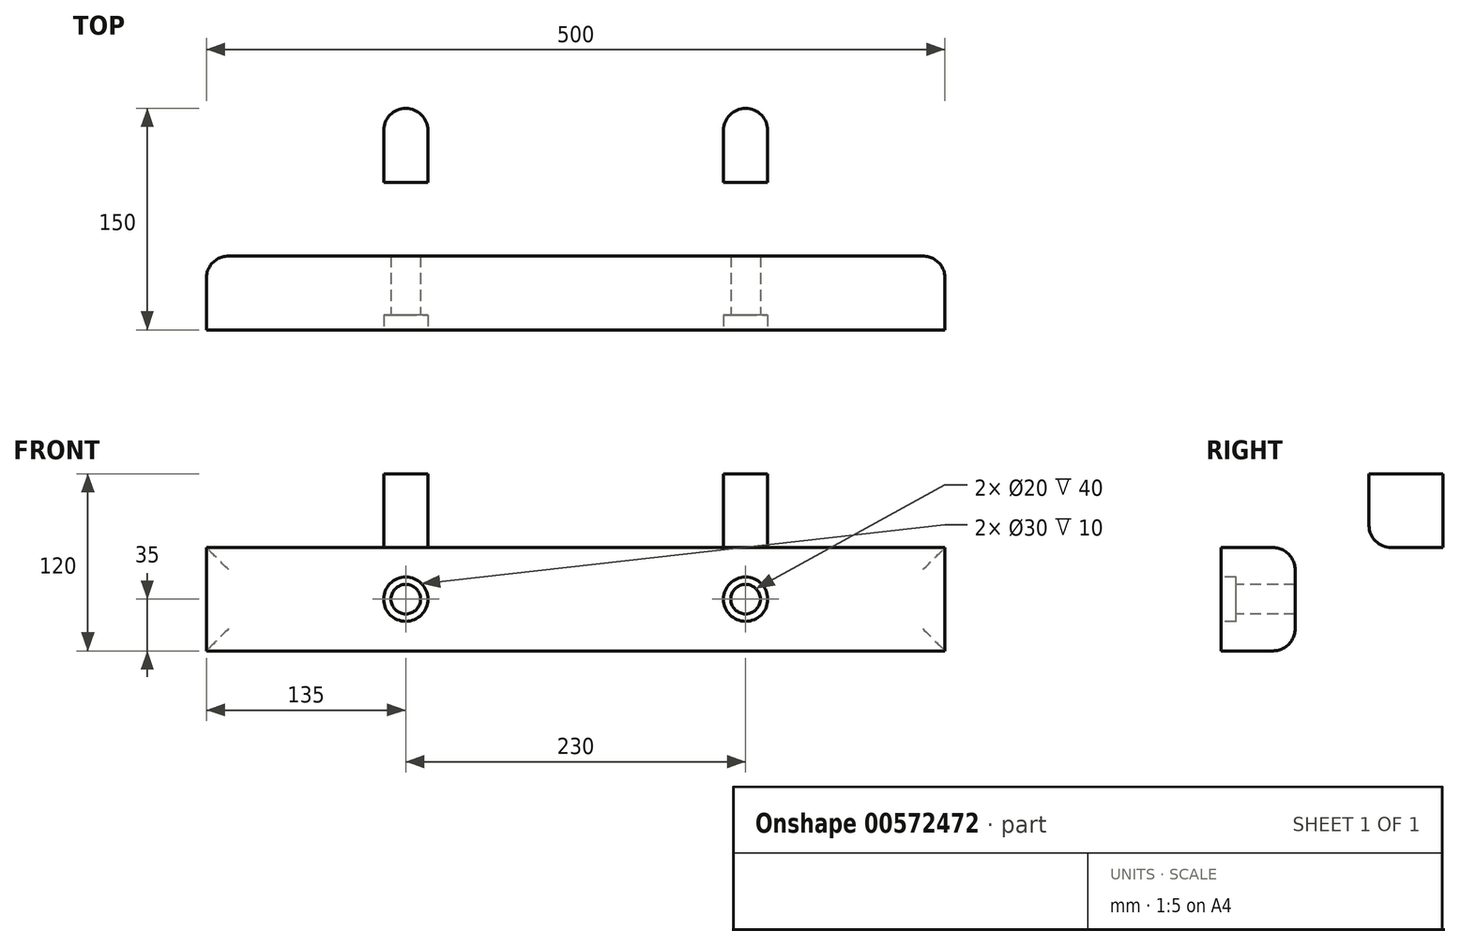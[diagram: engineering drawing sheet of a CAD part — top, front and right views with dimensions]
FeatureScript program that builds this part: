
annotation { "Feature Type Name" : "Feature", "Feature Type Description" : "" }
export const myFeature = defineFeature(function(context is Context, id is Id, definition is map)
    precondition{}
    {
        {
            var Q0;
            Q0=qCreatedBy(makeId("Top.planeOp"),FACE);
            var sketch = newSketch(context, id + "F0", { "sketchPlane" : qUnion([Q0])});
            skLineSegment(sketch, "E0.bottom", {"start": v(-250, 0) * mm, "end": v(250, 0) * mm});
            skLineSegment(sketch, "E0.top", {"start": v(-250, -50) * mm, "end": v(250, -50) * mm});
            skLineSegment(sketch, "E0.left", {"start": v(-250, 0) * mm, "end": v(-250, -50) * mm});
            skLineSegment(sketch, "E0.right", {"start": v(250, 0) * mm, "end": v(250, -50) * mm});
            skLineSegment(sketch, "E1.bottom", {"start": v(-130, 0) * mm, "end": v(-100, 0) * mm});
            skLineSegment(sketch, "E1.top", {"start": v(-130, 100) * mm, "end": v(-100, 100) * mm});
            skLineSegment(sketch, "E1.left", {"start": v(-130, 0) * mm, "end": v(-130, 100) * mm});
            skLineSegment(sketch, "E1.right", {"start": v(-100, 0) * mm, "end": v(-100, 100) * mm});
            skLineSegment(sketch, "E2.bottom", {"start": v(100, 0) * mm, "end": v(130, 0) * mm});
            skLineSegment(sketch, "E2.top", {"start": v(100, 100) * mm, "end": v(130, 100) * mm});
            skLineSegment(sketch, "E2.left", {"start": v(100, 0) * mm, "end": v(100, 100) * mm});
            skLineSegment(sketch, "E2.right", {"start": v(130, 0) * mm, "end": v(130, 100) * mm});
            skSolve(sketch);
        }
        {
            var Q0;
            Q0=makeQuery(id+"F0.imprint","IMPRINT",FACE,{"disambiguationData":[TD([[makeQuery(id+"F0.imprint","IMPRINT",EDGE,{"derivedFrom":sQuery(id+"F0.wireOp",EDGE,"E0.top")}),1.0]])]});
            var Q1;
            Q1=makeQuery(id+"F0.imprint","IMPRINT",FACE,{"disambiguationData":[TD([[makeQuery(id+"F0.imprint","IMPRINT",EDGE,{"derivedFrom":sQuery(id+"F0.wireOp",EDGE,"E1.bottom")}),1.0]])]});
            var Q2;
            Q2=makeQuery(id+"F0.imprint","IMPRINT",FACE,{"disambiguationData":[TD([[makeQuery(id+"F0.imprint","IMPRINT",EDGE,{"derivedFrom":sQuery(id+"F0.wireOp",EDGE,"E2.bottom")}),1.0]])]});
            extrude(context, id + "F1", {"entities" : qUnion([Q0, Q1, Q2]), "depth" : 70 * mm, "offsetDistance" : 25 * mm});
        }
        {
            var Q0;
            Q0=makeQuery(id+"F1.opExtrude","CAP_FACE",FACE,{"disambiguationData":[OSD([sQuery(id+"F0.wireOp",EDGE,"E0.bottom"),sQuery(id+"F0.wireOp",EDGE,"E0.top"),sQuery(id+"F0.wireOp",EDGE,"E0.left"),sQuery(id+"F0.wireOp",EDGE,"E0.right"),sQuery(id+"F0.wireOp",EDGE,"E1.top"),sQuery(id+"F0.wireOp",EDGE,"E1.left"),sQuery(id+"F0.wireOp",EDGE,"E1.right"),sQuery(id+"F0.wireOp",EDGE,"E2.top"),sQuery(id+"F0.wireOp",EDGE,"E2.left"),sQuery(id+"F0.wireOp",EDGE,"E2.right")])],"isStart":false});
            var sketch = newSketch(context, id + "F2", { "sketchPlane" : qUnion([Q0])});
            skLineSegment(sketch, "E3.bottom", {"start": v(-130, 100) * mm, "end": v(-100, 100) * mm});
            skLineSegment(sketch, "E3.top", {"start": v(-130, 50) * mm, "end": v(-100, 50) * mm});
            skLineSegment(sketch, "E3.left", {"start": v(-130, 100) * mm, "end": v(-130, 50) * mm});
            skLineSegment(sketch, "E3.right", {"start": v(-100, 100) * mm, "end": v(-100, 50) * mm});
            skLineSegment(sketch, "E4.bottom", {"start": v(100, 100) * mm, "end": v(130, 100) * mm});
            skLineSegment(sketch, "E4.top", {"start": v(100, 50) * mm, "end": v(130, 50) * mm});
            skLineSegment(sketch, "E4.left", {"start": v(100, 100) * mm, "end": v(100, 50) * mm});
            skLineSegment(sketch, "E4.right", {"start": v(130, 100) * mm, "end": v(130, 50) * mm});
            skSolve(sketch);
        }
        {
            var Q0;
            Q0=makeQuery(id+"F2.imprint","IMPRINT",FACE,{"disambiguationData":[TD([[makeQuery(id+"F2.imprint","IMPRINT",EDGE,{"derivedFrom":sQuery(id+"F2.wireOp",EDGE,"E3.bottom")}),-1.0]])]});
            var Q1;
            Q1=makeQuery(id+"F2.imprint","IMPRINT",FACE,{"disambiguationData":[TD([[makeQuery(id+"F2.imprint","IMPRINT",EDGE,{"derivedFrom":sQuery(id+"F2.wireOp",EDGE,"E4.bottom")}),-1.0]])]});
            extrude(context, id + "F3", {"entities" : qUnion([Q0, Q1]), "operationType" : NewBodyOperationType.ADD, "depth" : 50 * mm, "offsetDistance" : 25 * mm});
        }
        {
            var Q0;
            Q0=makeQuery(id+"F3.opExtrude","CAP_EDGE",EDGE,{"disambiguationData":[OSD([sQuery(id+"F2.wireOp",EDGE,"E3.top")])],"isStart":true});
            var Q1;
            Q1=makeQuery(id+"F3.opExtrude","CAP_EDGE",EDGE,{"disambiguationData":[OSD([sQuery(id+"F2.wireOp",EDGE,"E4.top")])],"isStart":true});
            var Q2;
            Q2=makeQuery(id+"F1.opExtrude","SWEPT_EDGE",EDGE,{"disambiguationData":[OSD([sQuery(id+"F0.wireOp",EDGE,"E0.bottom"),sQuery(id+"F0.wireOp",EDGE,"E2.bottom"),sQuery(id+"F0.wireOp",EDGE,"E2.left")])]});
            var Q3;
            Q3=makeQuery(id+"F1.opExtrude","SWEPT_EDGE",EDGE,{"disambiguationData":[OSD([sQuery(id+"F0.wireOp",EDGE,"E0.bottom"),sQuery(id+"F0.wireOp",EDGE,"E1.bottom"),sQuery(id+"F0.wireOp",EDGE,"E1.left")])]});
            var Q4;
            Q4=makeQuery(id+"F1.opExtrude","SWEPT_EDGE",EDGE,{"disambiguationData":[OSD([sQuery(id+"F0.wireOp",EDGE,"E0.bottom"),sQuery(id+"F0.wireOp",EDGE,"E1.bottom"),sQuery(id+"F0.wireOp",EDGE,"E1.right")])]});
            var Q5;
            Q5=makeQuery(id+"F1.opExtrude","SWEPT_EDGE",EDGE,{"disambiguationData":[OSD([sQuery(id+"F0.wireOp",EDGE,"E0.bottom"),sQuery(id+"F0.wireOp",EDGE,"E2.bottom"),sQuery(id+"F0.wireOp",EDGE,"E2.right")])]});
            var Q6;
            {var subQ0=sQuery(id+"F0.wireOp",EDGE,"E0.bottom");Q6=makeQuery(id+"F1.opExtrude","CAP_EDGE",EDGE,{"disambiguationData":[OSD([subQ0]),TDD([makeQuery(id+"F0.imprint","IMPRINT",EDGE,{"disambiguationData":[TD([[makeQuery(id+"F0.imprint","INTERSECT",VERTEX,{"derivedFrom":[subQ0,sQuery(id+"F0.wireOp",EDGE,"E1.bottom"),sQuery(id+"F0.wireOp",EDGE,"E1.right")]}),-1.0]])],"derivedFrom":subQ0})])],"isStart":false});}
            var Q7;
            Q7=makeQuery(id+"F1.opExtrude","CAP_EDGE",EDGE,{"disambiguationData":[OSD([sQuery(id+"F0.wireOp",EDGE,"E2.top")])],"isStart":true});
            var Q8;
            {var subQ0=sQuery(id+"F0.wireOp",EDGE,"E0.bottom");Q8=makeQuery(id+"F1.opExtrude","CAP_EDGE",EDGE,{"disambiguationData":[OSD([subQ0]),TDD([makeQuery(id+"F0.imprint","IMPRINT",EDGE,{"disambiguationData":[TD([[makeQuery(id+"F0.imprint","INTERSECT",VERTEX,{"derivedFrom":[subQ0,sQuery(id+"F0.wireOp",EDGE,"E0.right")]}),1.0]])],"derivedFrom":subQ0})])],"isStart":true});}
            var Q9;
            {var subQ0=sQuery(id+"F0.wireOp",EDGE,"E0.bottom");Q9=makeQuery(id+"F1.opExtrude","CAP_EDGE",EDGE,{"disambiguationData":[OSD([subQ0]),TDD([makeQuery(id+"F0.imprint","IMPRINT",EDGE,{"disambiguationData":[TD([[makeQuery(id+"F0.imprint","INTERSECT",VERTEX,{"derivedFrom":[subQ0,sQuery(id+"F0.wireOp",EDGE,"E0.right")]}),1.0]])],"derivedFrom":subQ0})])],"isStart":false});}
            var Q10;
            Q10=makeQuery(id+"F1.opExtrude","SWEPT_EDGE",EDGE,{"disambiguationData":[OSD([sQuery(id+"F0.wireOp",EDGE,"E0.bottom"),sQuery(id+"F0.wireOp",EDGE,"E0.right")])]});
            var Q11;
            Q11=makeQuery(id+"F3.boolean.opBoolean","MERGE",EDGE,{"derivedFrom":[makeQuery(id+"F1.opExtrude","SWEPT_EDGE",EDGE,{"disambiguationData":[OSD([sQuery(id+"F0.wireOp",EDGE,"E2.top"),sQuery(id+"F0.wireOp",EDGE,"E2.right")])]}),makeQuery(id+"F3.opExtrude","SWEPT_EDGE",EDGE,{"disambiguationData":[OSD([sQuery(id+"F2.wireOp",EDGE,"E4.bottom"),sQuery(id+"F2.wireOp",EDGE,"E4.right")])]})]});
            var Q12;
            Q12=makeQuery(id+"F3.boolean.opBoolean","MERGE",EDGE,{"derivedFrom":[makeQuery(id+"F1.opExtrude","SWEPT_EDGE",EDGE,{"disambiguationData":[OSD([sQuery(id+"F0.wireOp",EDGE,"E2.top"),sQuery(id+"F0.wireOp",EDGE,"E2.left")])]}),makeQuery(id+"F3.opExtrude","SWEPT_EDGE",EDGE,{"disambiguationData":[OSD([sQuery(id+"F2.wireOp",EDGE,"E4.bottom"),sQuery(id+"F2.wireOp",EDGE,"E4.left")])]})]});
            var Q13;
            {var subQ0=sQuery(id+"F0.wireOp",EDGE,"E0.bottom");Q13=makeQuery(id+"F1.opExtrude","CAP_EDGE",EDGE,{"disambiguationData":[OSD([subQ0]),TDD([makeQuery(id+"F0.imprint","IMPRINT",EDGE,{"disambiguationData":[TD([[makeQuery(id+"F0.imprint","INTERSECT",VERTEX,{"derivedFrom":[subQ0,sQuery(id+"F0.wireOp",EDGE,"E1.bottom"),sQuery(id+"F0.wireOp",EDGE,"E1.right")]}),-1.0]])],"derivedFrom":subQ0})])],"isStart":true});}
            var Q14;
            {var subQ0=sQuery(id+"F0.wireOp",EDGE,"E0.bottom");Q14=makeQuery(id+"F1.opExtrude","CAP_EDGE",EDGE,{"disambiguationData":[OSD([subQ0]),TDD([makeQuery(id+"F0.imprint","IMPRINT",EDGE,{"disambiguationData":[TD([[makeQuery(id+"F0.imprint","INTERSECT",VERTEX,{"derivedFrom":[subQ0,sQuery(id+"F0.wireOp",EDGE,"E0.left")]}),-1.0]])],"derivedFrom":subQ0})])],"isStart":true});}
            var Q15;
            Q15=makeQuery(id+"F1.opExtrude","SWEPT_EDGE",EDGE,{"disambiguationData":[OSD([sQuery(id+"F0.wireOp",EDGE,"E0.bottom"),sQuery(id+"F0.wireOp",EDGE,"E0.left")])]});
            var Q16;
            {var subQ0=sQuery(id+"F0.wireOp",EDGE,"E0.bottom");Q16=makeQuery(id+"F1.opExtrude","CAP_EDGE",EDGE,{"disambiguationData":[OSD([subQ0]),TDD([makeQuery(id+"F0.imprint","IMPRINT",EDGE,{"disambiguationData":[TD([[makeQuery(id+"F0.imprint","INTERSECT",VERTEX,{"derivedFrom":[subQ0,sQuery(id+"F0.wireOp",EDGE,"E0.left")]}),-1.0]])],"derivedFrom":subQ0})])],"isStart":false});}
            var Q17;
            Q17=makeQuery(id+"F3.boolean.opBoolean","MERGE",EDGE,{"derivedFrom":[makeQuery(id+"F1.opExtrude","SWEPT_EDGE",EDGE,{"disambiguationData":[OSD([sQuery(id+"F0.wireOp",EDGE,"E1.top"),sQuery(id+"F0.wireOp",EDGE,"E1.right")])]}),makeQuery(id+"F3.opExtrude","SWEPT_EDGE",EDGE,{"disambiguationData":[OSD([sQuery(id+"F2.wireOp",EDGE,"E3.bottom"),sQuery(id+"F2.wireOp",EDGE,"E3.right")])]})]});
            var Q18;
            Q18=makeQuery(id+"F1.opExtrude","CAP_EDGE",EDGE,{"disambiguationData":[OSD([sQuery(id+"F0.wireOp",EDGE,"E1.top")])],"isStart":true});
            var Q19;
            Q19=makeQuery(id+"F3.boolean.opBoolean","MERGE",EDGE,{"derivedFrom":[makeQuery(id+"F1.opExtrude","SWEPT_EDGE",EDGE,{"disambiguationData":[OSD([sQuery(id+"F0.wireOp",EDGE,"E1.top"),sQuery(id+"F0.wireOp",EDGE,"E1.left")])]}),makeQuery(id+"F3.opExtrude","SWEPT_EDGE",EDGE,{"disambiguationData":[OSD([sQuery(id+"F2.wireOp",EDGE,"E3.bottom"),sQuery(id+"F2.wireOp",EDGE,"E3.left")])]})]});
            fillet(context, id + "F4", {"entities" : qUnion([Q0, Q1, Q2, Q3, Q4, Q5, Q6, Q7, Q8, Q9, Q10, Q11, Q12, Q13, Q14, Q15, Q16, Q17, Q18, Q19]), "radius" : 15 * mm, "tangentPropagation" : true, "allowEdgeOverflow" : false});
        }
        {
            var Q0;
            Q0=makeQuery(id+"F1.opExtrude","SWEPT_FACE",FACE,{"disambiguationData":[OSD([sQuery(id+"F0.wireOp",EDGE,"E0.top")])]});
            var sketch = newSketch(context, id + "F5", { "sketchPlane" : qUnion([Q0])});
            skPoint(sketch, "E5.0", {"position": v(-115, 120) * mm});
            skPoint(sketch, "E6.0", {"position": v(115, 120) * mm});
            skPoint(sketch, "E7", {"position": v(-115, 35) * mm});
            skPoint(sketch, "E7.positionSnap0", {"position": v(-250, 35) * mm});
            skPoint(sketch, "E8", {"position": v(115, 35) * mm});
            skSolve(sketch);
        }
        {
            var Q0;
            Q0=sQuery(id+"F5.wireOp",VERTEX,"E7");
            var Q1;
            Q1=sQuery(id+"F5.wireOp",VERTEX,"E8");
            var Q2;
            Q2=makeQuery(id+"F1.opExtrude","SWEPT_BODY",BODY,{"disambiguationData":[OSD([sQuery(id+"F0.wireOp",EDGE,"E0.bottom"),sQuery(id+"F0.wireOp",EDGE,"E0.top"),sQuery(id+"F0.wireOp",EDGE,"E0.left"),sQuery(id+"F0.wireOp",EDGE,"E0.right"),sQuery(id+"F0.wireOp",EDGE,"E1.top"),sQuery(id+"F0.wireOp",EDGE,"E1.left"),sQuery(id+"F0.wireOp",EDGE,"E1.right"),sQuery(id+"F0.wireOp",EDGE,"E2.top"),sQuery(id+"F0.wireOp",EDGE,"E2.left"),sQuery(id+"F0.wireOp",EDGE,"E2.right")])]});
            hole(context, id + "F6", {"style" : HoleStyle.C_BORE, "endStyle" : HoleEndStyle.BLIND, "holeDiameter" : 20 * mm, "cBoreDiameter" : 30 * mm, "cBoreDepth" : 10 * mm, "holeDepth" : 50 * mm, "isTappedThrough" : true, "tappedDepth" : 12 * mm, "tapClearance" : 3, "locations" : qUnion([Q0, Q1]), "scope" : qUnion([Q2])});
        }
    });
